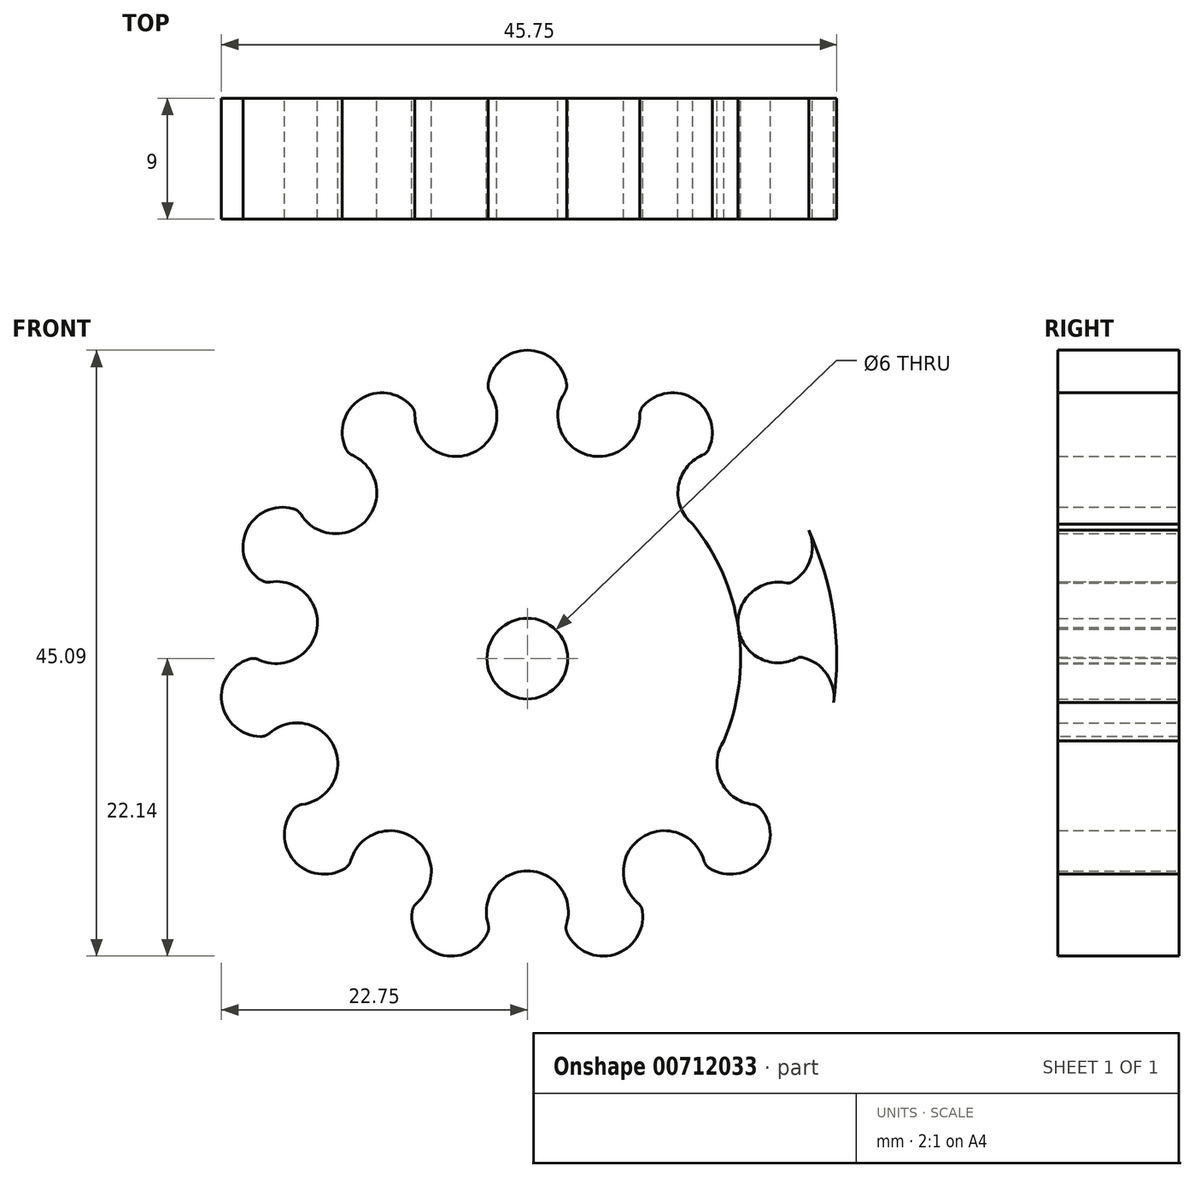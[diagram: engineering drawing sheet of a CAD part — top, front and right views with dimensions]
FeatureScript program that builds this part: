
annotation { "Feature Type Name" : "Feature", "Feature Type Description" : "" }
export const myFeature = defineFeature(function(context is Context, id is Id, definition is map)
    precondition{}
    {
        {
            var Q0;
            Q0=qCreatedBy(makeId("Front.planeOp"),FACE);
            var sketch = newSketch(context, id + "F0", { "sketchPlane" : qUnion([Q0])});
            skCircle(sketch, "E0", {"center": v(0, 0) * mm, "radius": 23 * mm});
            skArc(sketch, "E1", {"start": v(3, 20.2) * mm, "mid": v(0, 23) * mm, "end": v(-3, 20.2) * mm});
            skLineSegment(sketch, "E2", {"start": v(0, 0) * mm, "end": v(0, -23) * mm});
            skLineSegment(sketch, "E3", {"start": v(0, 23) * mm, "end": v(0, 23) * mm});
            skArc(sketch, "E4.1.7", {"start": v(-8.4, 18.61) * mm, "mid": v(-12.43, 19.35) * mm, "end": v(-13.44, 15.37) * mm});
            skArc(sketch, "E4.2.7", {"start": v(-17.13, 11.11) * mm, "mid": v(-20.92, 9.55) * mm, "end": v(-19.62, 5.67) * mm});
            skArc(sketch, "E4.3.7", {"start": v(-20.42, 0.09) * mm, "mid": v(-22.77, -3.27) * mm, "end": v(-19.57, -5.84) * mm});
            skArc(sketch, "E4.4.7", {"start": v(-17.22, -10.96) * mm, "mid": v(-17.38, -15.06) * mm, "end": v(-13.3, -15.49) * mm});
            skArc(sketch, "E4.5.7", {"start": v(-8.56, -18.54) * mm, "mid": v(-6.48, -22.07) * mm, "end": v(-2.82, -20.22) * mm});
            skArc(sketch, "E4.6.7", {"start": v(2.82, -20.22) * mm, "mid": v(6.48, -22.07) * mm, "end": v(8.56, -18.54) * mm});
            skArc(sketch, "E4.7.7", {"start": v(13.3, -15.49) * mm, "mid": v(17.38, -15.06) * mm, "end": v(17.22, -10.96) * mm});
            skCircle(sketch, "E5", {"center": v(0, 0) * mm, "radius": 15.85 * mm});
            skCircle(sketch, "E6", {"center": v(0, 0) * mm, "radius": 3 * mm});
            skArc(sketch, "E7.13.8.0", {"start": v(19.57, -5.84) * mm, "mid": v(22.77, -3.27) * mm, "end": v(20.42, 0.09) * mm});
            skArc(sketch, "E8.13.9.0", {"start": v(19.62, 5.67) * mm, "mid": v(20.92, 9.55) * mm, "end": v(17.13, 11.11) * mm});
            skArc(sketch, "E9.13.10.0", {"start": v(13.44, 15.37) * mm, "mid": v(12.43, 19.35) * mm, "end": v(8.4, 18.61) * mm});
            skArc(sketch, "E10", {"start": v(2.9, 19.87) * mm, "mid": v(4.47, 15.2) * mm, "end": v(8.3, 18.28) * mm});
            skArc(sketch, "E11.1.0", {"start": v(-8.3, 18.28) * mm, "mid": v(-4.47, 15.2) * mm, "end": v(-2.9, 19.87) * mm});
            skArc(sketch, "E11.2.0", {"start": v(-16.87, 10.89) * mm, "mid": v(-11.98, 10.38) * mm, "end": v(-13.18, 15.15) * mm});
            skArc(sketch, "E11.3.0", {"start": v(-20.08, 0.04) * mm, "mid": v(-15.69, 2.26) * mm, "end": v(-19.28, 5.62) * mm});
            skArc(sketch, "E11.4.0", {"start": v(-16.91, -10.82) * mm, "mid": v(-14.42, -6.58) * mm, "end": v(-19.25, -5.7) * mm});
            skArc(sketch, "E11.5.0", {"start": v(-8.38, -18.25) * mm, "mid": v(-8.57, -13.33) * mm, "end": v(-13.12, -15.2) * mm});
            skArc(sketch, "E11.6.0", {"start": v(2.82, -19.88) * mm, "mid": v(0, -15.85) * mm, "end": v(-2.82, -19.88) * mm});
            skArc(sketch, "E11.7.0", {"start": v(13.12, -15.2) * mm, "mid": v(8.57, -13.33) * mm, "end": v(8.38, -18.25) * mm});
            skArc(sketch, "E11.8.0", {"start": v(19.25, -5.7) * mm, "mid": v(14.42, -6.58) * mm, "end": v(16.91, -10.82) * mm});
            skArc(sketch, "E11.9.0", {"start": v(19.28, 5.62) * mm, "mid": v(15.69, 2.26) * mm, "end": v(20.08, 0.04) * mm});
            skArc(sketch, "E11.10.0", {"start": v(13.18, 15.15) * mm, "mid": v(11.98, 10.38) * mm, "end": v(16.87, 10.89) * mm});
            skPoint(sketch, "E12.visualSharp", {"position": v(3, 20) * mm});
            skArc(sketch, "E12.filletArc", {"start": v(2.9, 19.87) * mm, "mid": v(2.97, 20.02) * mm, "end": v(3, 20.2) * mm});
            skPoint(sketch, "E13.visualSharp", {"position": v(-3, 20) * mm});
            skArc(sketch, "E13.filletArc", {"start": v(-3, 20.2) * mm, "mid": v(-2.97, 20.02) * mm, "end": v(-2.9, 19.87) * mm});
            skPoint(sketch, "E14.visualSharp", {"position": v(-8.29, 18.45) * mm});
            skArc(sketch, "E14.filletArc", {"start": v(-8.3, 18.28) * mm, "mid": v(-8.32, 18.45) * mm, "end": v(-8.4, 18.61) * mm});
            skPoint(sketch, "E15.visualSharp", {"position": v(-13.34, 15.2) * mm});
            skArc(sketch, "E15.filletArc", {"start": v(-13.44, 15.37) * mm, "mid": v(-13.33, 15.24) * mm, "end": v(-13.18, 15.15) * mm});
            skPoint(sketch, "E16.visualSharp", {"position": v(-16.95, 11.04) * mm});
            skArc(sketch, "E16.filletArc", {"start": v(-16.87, 10.89) * mm, "mid": v(-16.98, 11.02) * mm, "end": v(-17.13, 11.11) * mm});
            skPoint(sketch, "E17.visualSharp", {"position": v(8.29, 18.45) * mm});
            skArc(sketch, "E17.filletArc", {"start": v(8.4, 18.61) * mm, "mid": v(8.32, 18.45) * mm, "end": v(8.3, 18.28) * mm});
            skPoint(sketch, "E18.visualSharp", {"position": v(13.34, 15.2) * mm});
            skArc(sketch, "E18.filletArc", {"start": v(13.18, 15.15) * mm, "mid": v(13.33, 15.24) * mm, "end": v(13.44, 15.37) * mm});
            skPoint(sketch, "E19.visualSharp", {"position": v(16.95, 11.04) * mm});
            skArc(sketch, "E19.filletArc", {"start": v(17.13, 11.11) * mm, "mid": v(16.98, 11.02) * mm, "end": v(16.87, 10.89) * mm});
            skPoint(sketch, "E20.visualSharp", {"position": v(19.44, 5.58) * mm});
            skArc(sketch, "E20.filletArc", {"start": v(19.28, 5.62) * mm, "mid": v(19.45, 5.61) * mm, "end": v(19.62, 5.67) * mm});
            skPoint(sketch, "E21.visualSharp", {"position": v(20.22, 0.12) * mm});
            skArc(sketch, "E21.filletArc", {"start": v(20.42, 0.09) * mm, "mid": v(20.24, 0.1) * mm, "end": v(20.08, 0.04) * mm});
            skPoint(sketch, "E22.visualSharp", {"position": v(19.37, -5.82) * mm});
            skArc(sketch, "E22.filletArc", {"start": v(19.25, -5.7) * mm, "mid": v(19.4, -5.8) * mm, "end": v(19.57, -5.84) * mm});
            skPoint(sketch, "E23.visualSharp", {"position": v(17.08, -10.83) * mm});
            skArc(sketch, "E23.filletArc", {"start": v(17.22, -10.96) * mm, "mid": v(17.08, -10.87) * mm, "end": v(16.91, -10.82) * mm});
            skPoint(sketch, "E24.visualSharp", {"position": v(13.15, -15.36) * mm});
            skArc(sketch, "E24.filletArc", {"start": v(13.12, -15.2) * mm, "mid": v(13.19, -15.36) * mm, "end": v(13.3, -15.49) * mm});
            skPoint(sketch, "E25.visualSharp", {"position": v(8.51, -18.34) * mm});
            skArc(sketch, "E25.filletArc", {"start": v(8.56, -18.54) * mm, "mid": v(8.5, -18.38) * mm, "end": v(8.38, -18.25) * mm});
            skPoint(sketch, "E26.visualSharp", {"position": v(2.76, -20.04) * mm});
            skArc(sketch, "E26.filletArc", {"start": v(2.82, -19.88) * mm, "mid": v(2.79, -20.05) * mm, "end": v(2.82, -20.22) * mm});
            skPoint(sketch, "E27.visualSharp", {"position": v(-2.76, -20.04) * mm});
            skArc(sketch, "E27.filletArc", {"start": v(-2.82, -20.22) * mm, "mid": v(-2.79, -20.05) * mm, "end": v(-2.82, -19.88) * mm});
            skPoint(sketch, "E28.visualSharp", {"position": v(-8.51, -18.34) * mm});
            skArc(sketch, "E28.filletArc", {"start": v(-8.38, -18.25) * mm, "mid": v(-8.5, -18.38) * mm, "end": v(-8.56, -18.54) * mm});
            skPoint(sketch, "E29.visualSharp", {"position": v(-13.15, -15.36) * mm});
            skArc(sketch, "E29.filletArc", {"start": v(-13.3, -15.49) * mm, "mid": v(-13.19, -15.36) * mm, "end": v(-13.12, -15.2) * mm});
            skPoint(sketch, "E30.visualSharp", {"position": v(-17.08, -10.83) * mm});
            skArc(sketch, "E30.filletArc", {"start": v(-16.91, -10.82) * mm, "mid": v(-17.08, -10.87) * mm, "end": v(-17.22, -10.96) * mm});
            skPoint(sketch, "E31.visualSharp", {"position": v(-19.37, -5.82) * mm});
            skArc(sketch, "E31.filletArc", {"start": v(-19.57, -5.84) * mm, "mid": v(-19.4, -5.8) * mm, "end": v(-19.25, -5.7) * mm});
            skPoint(sketch, "E32.visualSharp", {"position": v(-20.22, 0.12) * mm});
            skArc(sketch, "E32.filletArc", {"start": v(-20.08, 0.04) * mm, "mid": v(-20.24, 0.1) * mm, "end": v(-20.42, 0.09) * mm});
            skPoint(sketch, "E33.visualSharp", {"position": v(-19.44, 5.58) * mm});
            skArc(sketch, "E33.filletArc", {"start": v(-19.62, 5.67) * mm, "mid": v(-19.45, 5.61) * mm, "end": v(-19.28, 5.62) * mm});
            skSolve(sketch);
        }
        {
            var Q0;
            {var subQ1=sQuery(id+"F0.wireOp",EDGE,"E4.1.2");Q0=makeQuery(id+"F0.imprint","IMPRINT",FACE,{"disambiguationData":[TD([[makeQuery(id+"F0.imprint","IMPRINT",EDGE,{"derivedFrom":subQ1}),1.0]])]});}
            var Q1;
            {var subQ1=sQuery(id+"F0.wireOp",EDGE,"E4.2.2");Q1=makeQuery(id+"F0.imprint","IMPRINT",FACE,{"disambiguationData":[TD([[makeQuery(id+"F0.imprint","IMPRINT",EDGE,{"derivedFrom":subQ1}),1.0]])]});}
            var Q2;
            {var subQ1=sQuery(id+"F0.wireOp",EDGE,"E4.3.2");Q2=makeQuery(id+"F0.imprint","IMPRINT",FACE,{"disambiguationData":[TD([[makeQuery(id+"F0.imprint","IMPRINT",EDGE,{"derivedFrom":subQ1}),1.0]])]});}
            var Q3;
            {var subQ1=sQuery(id+"F0.wireOp",EDGE,"E4.4.2");Q3=makeQuery(id+"F0.imprint","IMPRINT",FACE,{"disambiguationData":[TD([[makeQuery(id+"F0.imprint","IMPRINT",EDGE,{"derivedFrom":subQ1}),1.0]])]});}
            var Q4;
            {var subQ1=sQuery(id+"F0.wireOp",EDGE,"E4.5.2");Q4=makeQuery(id+"F0.imprint","IMPRINT",FACE,{"disambiguationData":[TD([[makeQuery(id+"F0.imprint","IMPRINT",EDGE,{"derivedFrom":subQ1}),1.0]])]});}
            var Q5;
            {var subQ1=sQuery(id+"F0.wireOp",EDGE,"E4.6.2");Q5=makeQuery(id+"F0.imprint","IMPRINT",FACE,{"disambiguationData":[TD([[makeQuery(id+"F0.imprint","IMPRINT",EDGE,{"derivedFrom":subQ1}),1.0]])]});}
            var Q6;
            {var subQ1=sQuery(id+"F0.wireOp",EDGE,"E4.7.2");Q6=makeQuery(id+"F0.imprint","IMPRINT",FACE,{"disambiguationData":[TD([[makeQuery(id+"F0.imprint","IMPRINT",EDGE,{"derivedFrom":subQ1}),1.0]])]});}
            var Q7;
            {var subQ1=sQuery(id+"F0.wireOp",EDGE,"E4.8.2");Q7=makeQuery(id+"F0.imprint","IMPRINT",FACE,{"disambiguationData":[TD([[makeQuery(id+"F0.imprint","IMPRINT",EDGE,{"derivedFrom":subQ1}),1.0]])]});}
            var Q8;
            {var subQ1=sQuery(id+"F0.wireOp",EDGE,"064e12d8-6572-4041-806d-f88136f2c4dc");Q8=makeQuery(id+"F0.imprint","IMPRINT",FACE,{"disambiguationData":[TD([[makeQuery(id+"F0.imprint","IMPRINT",EDGE,{"derivedFrom":subQ1}),1.0]])]});}
            var Q9;
            Q9=makeQuery(id+"F0.imprint","IMPRINT",FACE,{"disambiguationData":[TD([[makeQuery(id+"F0.imprint","IMPRINT",EDGE,{"derivedFrom":sQuery(id+"F0.wireOp",EDGE,"E6")}),-1.0]])]});
            var Q10;
            {var subQ0=sQuery(id+"F0.wireOp",EDGE,"E4.4.3");Q10=makeQuery(id+"F0.imprint","IMPRINT",FACE,{"disambiguationData":[TD([[makeQuery(id+"F0.imprint","IMPRINT",EDGE,{"derivedFrom":subQ0}),-1.0]])]});}
            var Q11;
            {var subQ5=sQuery(id+"F0.wireOp",EDGE,"E7.2.8.0");Q11=makeQuery(id+"F0.imprint","IMPRINT",FACE,{"disambiguationData":[TD([[makeQuery(id+"F0.imprint","IMPRINT",EDGE,{"derivedFrom":subQ5}),1.0]])]});}
            var Q12;
            {var subQ0=sQuery(id+"F0.wireOp",EDGE,"E4.5.3");Q12=makeQuery(id+"F0.imprint","IMPRINT",FACE,{"disambiguationData":[TD([[makeQuery(id+"F0.imprint","IMPRINT",EDGE,{"derivedFrom":subQ0}),-1.0]])]});}
            var Q13;
            {var subQ1=sQuery(id+"F0.wireOp",EDGE,"E8.2.9.0");Q13=makeQuery(id+"F0.imprint","IMPRINT",FACE,{"disambiguationData":[TD([[makeQuery(id+"F0.imprint","IMPRINT",EDGE,{"derivedFrom":subQ1}),1.0]])]});}
            var Q14;
            {var subQ2=sQuery(id+"F0.wireOp",EDGE,"E9.2.10.0");Q14=makeQuery(id+"F0.imprint","IMPRINT",FACE,{"disambiguationData":[TD([[makeQuery(id+"F0.imprint","IMPRINT",EDGE,{"derivedFrom":subQ2}),1.0]])]});}
            var Q15;
            {var subQ0=sQuery(id+"F0.wireOp",EDGE,"E11.9.0");var subQ3=sQuery(id+"F0.wireOp",EDGE,"E5");var subQ4=makeQuery(id+"F0.imprint","INTERSECT",VERTEX,{"disambiguationData":[OD(0.0)],"derivedFrom":[subQ3,subQ0]});Q15=makeQuery(id+"F0.imprint","IMPRINT",FACE,{"disambiguationData":[TD([[makeQuery(id+"F0.imprint","IMPRINT",EDGE,{"disambiguationData":[TD([[subQ4,-1.0]])],"derivedFrom":subQ3}),-1.0]])]});}
            var Q16;
            {var subQ3=sQuery(id+"F0.wireOp",EDGE,"E5");var subQ6=sQuery(id+"F0.wireOp",EDGE,"E11.10.0");var subQ8=makeQuery(id+"F0.imprint","INTERSECT",VERTEX,{"disambiguationData":[OD(1.0)],"derivedFrom":[subQ3,subQ6]});Q16=makeQuery(id+"F0.imprint","IMPRINT",FACE,{"disambiguationData":[TD([[makeQuery(id+"F0.imprint","IMPRINT",EDGE,{"disambiguationData":[TD([[subQ8,-1.0]])],"derivedFrom":subQ3}),-1.0]])]});}
            var Q17;
            {var subQ0=sQuery(id+"F0.wireOp",EDGE,"E10");var subQ1=sQuery(id+"F0.wireOp",EDGE,"E1");var subQ2=makeQuery(id+"F0.imprint","INTERSECT",VERTEX,{"derivedFrom":[subQ1,subQ0]});Q17=makeQuery(id+"F0.imprint","IMPRINT",FACE,{"disambiguationData":[TD([[makeQuery(id+"F0.imprint","IMPRINT",EDGE,{"disambiguationData":[TD([[subQ2,-1.0]])],"derivedFrom":subQ1}),1.0]])]});}
            var Q18;
            {var subQ0=sQuery(id+"F0.wireOp",EDGE,"E11.1.0");var subQ1=sQuery(id+"F0.wireOp",EDGE,"E4.1.7");var subQ2=makeQuery(id+"F0.imprint","INTERSECT",VERTEX,{"derivedFrom":[subQ1,subQ0]});Q18=makeQuery(id+"F0.imprint","IMPRINT",FACE,{"disambiguationData":[TD([[makeQuery(id+"F0.imprint","IMPRINT",EDGE,{"disambiguationData":[TD([[subQ2,-1.0]])],"derivedFrom":subQ1}),1.0]])]});}
            var Q19;
            {var subQ0=sQuery(id+"F0.wireOp",EDGE,"E11.2.0");var subQ1=sQuery(id+"F0.wireOp",EDGE,"E4.2.7");var subQ2=makeQuery(id+"F0.imprint","INTERSECT",VERTEX,{"derivedFrom":[subQ1,subQ0]});Q19=makeQuery(id+"F0.imprint","IMPRINT",FACE,{"disambiguationData":[TD([[makeQuery(id+"F0.imprint","IMPRINT",EDGE,{"disambiguationData":[TD([[subQ2,-1.0]])],"derivedFrom":subQ1}),1.0]])]});}
            var Q20;
            {var subQ0=sQuery(id+"F0.wireOp",EDGE,"E11.3.0");var subQ1=sQuery(id+"F0.wireOp",EDGE,"E4.3.7");var subQ2=makeQuery(id+"F0.imprint","INTERSECT",VERTEX,{"derivedFrom":[subQ1,subQ0]});Q20=makeQuery(id+"F0.imprint","IMPRINT",FACE,{"disambiguationData":[TD([[makeQuery(id+"F0.imprint","IMPRINT",EDGE,{"disambiguationData":[TD([[subQ2,-1.0]])],"derivedFrom":subQ1}),1.0]])]});}
            var Q21;
            {var subQ0=sQuery(id+"F0.wireOp",EDGE,"E11.4.0");var subQ5=sQuery(id+"F0.wireOp",EDGE,"E4.4.7");var subQ8=makeQuery(id+"F0.imprint","INTERSECT",VERTEX,{"derivedFrom":[subQ5,subQ0]});Q21=makeQuery(id+"F0.imprint","IMPRINT",FACE,{"disambiguationData":[TD([[makeQuery(id+"F0.imprint","IMPRINT",EDGE,{"disambiguationData":[TD([[subQ8,-1.0]])],"derivedFrom":subQ5}),1.0]])]});}
            var Q22;
            {var subQ0=sQuery(id+"F0.wireOp",EDGE,"E11.5.0");var subQ1=sQuery(id+"F0.wireOp",EDGE,"E4.5.7");var subQ2=makeQuery(id+"F0.imprint","INTERSECT",VERTEX,{"derivedFrom":[subQ1,subQ0]});Q22=makeQuery(id+"F0.imprint","IMPRINT",FACE,{"disambiguationData":[TD([[makeQuery(id+"F0.imprint","IMPRINT",EDGE,{"disambiguationData":[TD([[subQ2,-1.0]])],"derivedFrom":subQ1}),1.0]])]});}
            var Q23;
            {var subQ0=sQuery(id+"F0.wireOp",EDGE,"E11.6.0");var subQ1=sQuery(id+"F0.wireOp",EDGE,"E4.6.7");var subQ2=makeQuery(id+"F0.imprint","INTERSECT",VERTEX,{"derivedFrom":[subQ1,subQ0]});Q23=makeQuery(id+"F0.imprint","IMPRINT",FACE,{"disambiguationData":[TD([[makeQuery(id+"F0.imprint","IMPRINT",EDGE,{"disambiguationData":[TD([[subQ2,-1.0]])],"derivedFrom":subQ1}),1.0]])]});}
            var Q24;
            {var subQ0=sQuery(id+"F0.wireOp",EDGE,"E11.7.0");var subQ1=sQuery(id+"F0.wireOp",EDGE,"E4.7.7");var subQ2=makeQuery(id+"F0.imprint","INTERSECT",VERTEX,{"derivedFrom":[subQ1,subQ0]});Q24=makeQuery(id+"F0.imprint","IMPRINT",FACE,{"disambiguationData":[TD([[makeQuery(id+"F0.imprint","IMPRINT",EDGE,{"disambiguationData":[TD([[subQ2,-1.0]])],"derivedFrom":subQ1}),1.0]])]});}
            var Q25;
            {var subQ3=sQuery(id+"F0.wireOp",EDGE,"E5");var subQ5=sQuery(id+"F0.wireOp",EDGE,"E11.9.0");var subQ6=makeQuery(id+"F0.imprint","INTERSECT",VERTEX,{"disambiguationData":[OD(1.0)],"derivedFrom":[subQ3,subQ5]});Q25=makeQuery(id+"F0.imprint","IMPRINT",FACE,{"disambiguationData":[TD([[makeQuery(id+"F0.imprint","IMPRINT",EDGE,{"disambiguationData":[TD([[subQ6,1.0]])],"derivedFrom":subQ3}),-1.0]])]});}
            extrude(context, id + "F1", {"entities" : qUnion([Q0, Q1, Q2, Q3, Q4, Q5, Q6, Q7, Q8, Q9, Q10, Q11, Q12, Q13, Q14, Q15, Q16, Q17, Q18, Q19, Q20, Q21, Q22, Q23, Q24, Q25]), "depth" : 9 * mm, "offsetDistance" : 25 * mm});
        }
        {
            var Q0;
            Q0=makeQuery(id+"F1.opExtrude","CAP_FACE",FACE,{"disambiguationData":[OSD([sQuery(id+"F0.wireOp",EDGE,"E1"),sQuery(id+"F0.wireOp",EDGE,"E4.1.7"),sQuery(id+"F0.wireOp",EDGE,"E4.2.7"),sQuery(id+"F0.wireOp",EDGE,"E4.3.7"),sQuery(id+"F0.wireOp",EDGE,"E4.4.7"),sQuery(id+"F0.wireOp",EDGE,"E4.5.7"),sQuery(id+"F0.wireOp",EDGE,"E4.6.7"),sQuery(id+"F0.wireOp",EDGE,"E4.7.7"),sQuery(id+"F0.wireOp",EDGE,"E6"),sQuery(id+"F0.wireOp",EDGE,"E7.13.8.0"),sQuery(id+"F0.wireOp",EDGE,"E8.13.9.0"),sQuery(id+"F0.wireOp",EDGE,"E9.13.10.0"),sQuery(id+"F0.wireOp",EDGE,"E10"),sQuery(id+"F0.wireOp",EDGE,"E11.1.0"),sQuery(id+"F0.wireOp",EDGE,"E11.2.0"),sQuery(id+"F0.wireOp",EDGE,"E11.3.0"),sQuery(id+"F0.wireOp",EDGE,"E11.4.0"),sQuery(id+"F0.wireOp",EDGE,"E11.5.0"),sQuery(id+"F0.wireOp",EDGE,"E11.6.0"),sQuery(id+"F0.wireOp",EDGE,"E11.7.0"),sQuery(id+"F0.wireOp",EDGE,"E11.8.0"),sQuery(id+"F0.wireOp",EDGE,"E11.9.0"),sQuery(id+"F0.wireOp",EDGE,"E11.10.0"),sQuery(id+"F0.wireOp",EDGE,"E12.filletArc"),sQuery(id+"F0.wireOp",EDGE,"E13.filletArc"),sQuery(id+"F0.wireOp",EDGE,"E14.filletArc"),sQuery(id+"F0.wireOp",EDGE,"E15.filletArc"),sQuery(id+"F0.wireOp",EDGE,"E16.filletArc"),sQuery(id+"F0.wireOp",EDGE,"E17.filletArc"),sQuery(id+"F0.wireOp",EDGE,"E18.filletArc"),sQuery(id+"F0.wireOp",EDGE,"E19.filletArc"),sQuery(id+"F0.wireOp",EDGE,"E20.filletArc"),sQuery(id+"F0.wireOp",EDGE,"E21.filletArc"),sQuery(id+"F0.wireOp",EDGE,"E22.filletArc"),sQuery(id+"F0.wireOp",EDGE,"E23.filletArc"),sQuery(id+"F0.wireOp",EDGE,"E24.filletArc"),sQuery(id+"F0.wireOp",EDGE,"E25.filletArc"),sQuery(id+"F0.wireOp",EDGE,"E26.filletArc"),sQuery(id+"F0.wireOp",EDGE,"E27.filletArc"),sQuery(id+"F0.wireOp",EDGE,"E28.filletArc"),sQuery(id+"F0.wireOp",EDGE,"E29.filletArc"),sQuery(id+"F0.wireOp",EDGE,"E30.filletArc"),sQuery(id+"F0.wireOp",EDGE,"E31.filletArc"),sQuery(id+"F0.wireOp",EDGE,"E32.filletArc"),sQuery(id+"F0.wireOp",EDGE,"E33.filletArc")])],"isStart":true});
            var sketch = newSketch(context, id + "F2", { "sketchPlane" : qUnion([Q0])});
            skArc(sketch, "E34.0", {"start": v(-2.9, 19.87) * mm, "mid": v(-4.47, 15.2) * mm, "end": v(-8.3, 18.28) * mm});
            skArc(sketch, "E35.0", {"start": v(-3, 20.2) * mm, "mid": v(0, 23) * mm, "end": v(3, 20.2) * mm});
            skArc(sketch, "E36.0", {"start": v(8.3, 18.28) * mm, "mid": v(4.47, 15.2) * mm, "end": v(2.9, 19.87) * mm});
            skArc(sketch, "E37.0", {"start": v(8.4, 18.61) * mm, "mid": v(12.43, 19.35) * mm, "end": v(13.44, 15.37) * mm});
            skArc(sketch, "E38.0", {"start": v(16.87, 10.89) * mm, "mid": v(11.98, 10.38) * mm, "end": v(13.18, 15.15) * mm});
            skArc(sketch, "E39.0", {"start": v(17.13, 11.11) * mm, "mid": v(20.92, 9.55) * mm, "end": v(19.62, 5.67) * mm});
            skArc(sketch, "E40.0", {"start": v(20.08, 0.04) * mm, "mid": v(15.69, 2.26) * mm, "end": v(19.28, 5.62) * mm});
            skArc(sketch, "E41.0", {"start": v(20.42, 0.09) * mm, "mid": v(22.77, -3.27) * mm, "end": v(19.57, -5.84) * mm});
            skArc(sketch, "E42.0", {"start": v(16.91, -10.82) * mm, "mid": v(14.42, -6.58) * mm, "end": v(19.25, -5.7) * mm});
            skArc(sketch, "E43.0", {"start": v(17.22, -10.96) * mm, "mid": v(17.38, -15.06) * mm, "end": v(13.3, -15.49) * mm});
            skArc(sketch, "E44.0", {"start": v(8.38, -18.25) * mm, "mid": v(8.57, -13.33) * mm, "end": v(13.12, -15.2) * mm});
            skArc(sketch, "E45.0", {"start": v(8.56, -18.54) * mm, "mid": v(6.48, -22.07) * mm, "end": v(2.82, -20.22) * mm});
            skArc(sketch, "E46.0", {"start": v(-2.82, -19.88) * mm, "mid": v(0, -15.85) * mm, "end": v(2.82, -19.88) * mm});
            skArc(sketch, "E47.0", {"start": v(-2.82, -20.22) * mm, "mid": v(-6.48, -22.07) * mm, "end": v(-8.56, -18.54) * mm});
            skArc(sketch, "E48.0", {"start": v(-13.12, -15.2) * mm, "mid": v(-8.57, -13.33) * mm, "end": v(-8.38, -18.25) * mm});
            skArc(sketch, "E49.0", {"start": v(-13.3, -15.49) * mm, "mid": v(-17.38, -15.06) * mm, "end": v(-17.22, -10.96) * mm});
            skArc(sketch, "E50.0", {"start": v(-19.25, -5.7) * mm, "mid": v(-14.42, -6.58) * mm, "end": v(-16.91, -10.82) * mm});
            skArc(sketch, "E51.0", {"start": v(-19.57, -5.84) * mm, "mid": v(-22.77, -3.27) * mm, "end": v(-20.42, 0.09) * mm});
            skArc(sketch, "E52.0", {"start": v(-19.28, 5.62) * mm, "mid": v(-15.69, 2.26) * mm, "end": v(-20.08, 0.04) * mm});
            skArc(sketch, "E53.0", {"start": v(-13.18, 15.15) * mm, "mid": v(-11.98, 10.38) * mm, "end": v(-16.87, 10.89) * mm});
            skArc(sketch, "E54.0", {"start": v(-13.44, 15.37) * mm, "mid": v(-12.43, 19.35) * mm, "end": v(-8.4, 18.61) * mm});
            skArc(sketch, "E55.0", {"start": v(-19.62, 5.67) * mm, "mid": v(-20.92, 9.55) * mm, "end": v(-17.13, 11.11) * mm});
            skArc(sketch, "E56.0", {"start": v(-13.18, 15.15) * mm, "mid": v(-13.33, 15.24) * mm, "end": v(-13.44, 15.37) * mm});
            skArc(sketch, "E57.0", {"start": v(-8.4, 18.61) * mm, "mid": v(-8.32, 18.45) * mm, "end": v(-8.3, 18.28) * mm});
            skPoint(sketch, "E58.0", {"position": v(-2.97, 20.02) * mm});
            skArc(sketch, "E59.0", {"start": v(3, 20.2) * mm, "mid": v(2.97, 20.02) * mm, "end": v(2.9, 19.87) * mm});
            skArc(sketch, "E60.0", {"start": v(13.44, 15.37) * mm, "mid": v(13.33, 15.24) * mm, "end": v(13.18, 15.15) * mm});
            skArc(sketch, "E61.0", {"start": v(8.3, 18.28) * mm, "mid": v(8.32, 18.45) * mm, "end": v(8.4, 18.61) * mm});
            skPoint(sketch, "E62.0", {"position": v(16.98, 11.02) * mm});
            skArc(sketch, "E63.0", {"start": v(19.62, 5.67) * mm, "mid": v(19.45, 5.61) * mm, "end": v(19.28, 5.62) * mm});
            skArc(sketch, "E64.0", {"start": v(16.87, 10.89) * mm, "mid": v(16.98, 11.02) * mm, "end": v(17.13, 11.11) * mm});
            skArc(sketch, "E65.0", {"start": v(-2.9, 19.87) * mm, "mid": v(-2.97, 20.02) * mm, "end": v(-3, 20.2) * mm});
            skArc(sketch, "E66.0", {"start": v(-19.28, 5.62) * mm, "mid": v(-19.45, 5.61) * mm, "end": v(-19.62, 5.67) * mm});
            skArc(sketch, "E67.0", {"start": v(-17.13, 11.11) * mm, "mid": v(-16.98, 11.02) * mm, "end": v(-16.87, 10.89) * mm});
            skArc(sketch, "E68.0", {"start": v(-19.25, -5.7) * mm, "mid": v(-19.4, -5.8) * mm, "end": v(-19.57, -5.84) * mm});
            skArc(sketch, "E69.0", {"start": v(-20.42, 0.09) * mm, "mid": v(-20.24, 0.1) * mm, "end": v(-20.08, 0.04) * mm});
            skArc(sketch, "E70.0", {"start": v(-17.22, -10.96) * mm, "mid": v(-17.08, -10.87) * mm, "end": v(-16.91, -10.82) * mm});
            skArc(sketch, "E71.0", {"start": v(-13.12, -15.2) * mm, "mid": v(-13.19, -15.36) * mm, "end": v(-13.3, -15.49) * mm});
            skArc(sketch, "E72.0", {"start": v(-8.56, -18.54) * mm, "mid": v(-8.5, -18.38) * mm, "end": v(-8.38, -18.25) * mm});
            skArc(sketch, "E73.0", {"start": v(-2.82, -19.88) * mm, "mid": v(-2.79, -20.05) * mm, "end": v(-2.82, -20.22) * mm});
            skArc(sketch, "E74.0", {"start": v(2.82, -20.22) * mm, "mid": v(2.79, -20.05) * mm, "end": v(2.82, -19.88) * mm});
            skArc(sketch, "E75.0", {"start": v(8.38, -18.25) * mm, "mid": v(8.5, -18.38) * mm, "end": v(8.56, -18.54) * mm});
            skArc(sketch, "E76.0", {"start": v(13.3, -15.49) * mm, "mid": v(13.19, -15.36) * mm, "end": v(13.12, -15.2) * mm});
            skArc(sketch, "E77.0", {"start": v(16.91, -10.82) * mm, "mid": v(17.08, -10.87) * mm, "end": v(17.22, -10.96) * mm});
            skArc(sketch, "E78.0", {"start": v(19.57, -5.84) * mm, "mid": v(19.4, -5.8) * mm, "end": v(19.25, -5.7) * mm});
            skArc(sketch, "E79.0", {"start": v(20.08, 0.04) * mm, "mid": v(20.24, 0.1) * mm, "end": v(20.42, 0.09) * mm});
            skArc(sketch, "E80.0", {"start": v(-2.95, 20.02) * mm, "mid": v(0, 22.95) * mm, "end": v(2.95, 20.02) * mm});
            skArc(sketch, "E80.1", {"start": v(8.34, 18.43) * mm, "mid": v(4.45, 15.16) * mm, "end": v(2.95, 20.02) * mm});
            skArc(sketch, "E80.2", {"start": v(8.34, 18.43) * mm, "mid": v(12.4, 19.3) * mm, "end": v(13.3, 15.25) * mm});
            skArc(sketch, "E80.3", {"start": v(16.98, 11) * mm, "mid": v(11.94, 10.35) * mm, "end": v(13.3, 15.25) * mm});
            skArc(sketch, "E80.4", {"start": v(16.98, 11) * mm, "mid": v(20.88, 9.53) * mm, "end": v(19.43, 5.63) * mm});
            skArc(sketch, "E80.5", {"start": v(-2.95, 20.02) * mm, "mid": v(-4.45, 15.16) * mm, "end": v(-8.34, 18.43) * mm});
            skArc(sketch, "E80.6", {"start": v(20.23, 0.07) * mm, "mid": v(15.64, 2.25) * mm, "end": v(19.43, 5.63) * mm});
            skArc(sketch, "E80.7", {"start": v(20.23, 0.07) * mm, "mid": v(22.72, -3.27) * mm, "end": v(19.4, -5.77) * mm});
            skArc(sketch, "E80.8", {"start": v(17.06, -10.88) * mm, "mid": v(14.37, -6.56) * mm, "end": v(19.4, -5.77) * mm});
            skArc(sketch, "E80.9", {"start": v(17.06, -10.88) * mm, "mid": v(17.34, -15.03) * mm, "end": v(13.2, -15.34) * mm});
            skArc(sketch, "E80.10", {"start": v(8.47, -18.38) * mm, "mid": v(8.54, -13.3) * mm, "end": v(13.2, -15.34) * mm});
            skArc(sketch, "E80.11", {"start": v(8.47, -18.38) * mm, "mid": v(6.47, -22.02) * mm, "end": v(2.8, -20.04) * mm});
            skArc(sketch, "E80.12", {"start": v(-19.43, 5.63) * mm, "mid": v(-15.64, 2.25) * mm, "end": v(-20.23, 0.07) * mm});
            skArc(sketch, "E80.13", {"start": v(-19.43, 5.63) * mm, "mid": v(-20.88, 9.53) * mm, "end": v(-16.98, 11) * mm});
            skArc(sketch, "E80.14", {"start": v(-13.3, 15.25) * mm, "mid": v(-11.94, 10.35) * mm, "end": v(-16.98, 11) * mm});
            skArc(sketch, "E80.15", {"start": v(-13.3, 15.25) * mm, "mid": v(-12.4, 19.3) * mm, "end": v(-8.34, 18.43) * mm});
            skArc(sketch, "E80.16", {"start": v(-19.4, -5.77) * mm, "mid": v(-22.72, -3.27) * mm, "end": v(-20.23, 0.07) * mm});
            skArc(sketch, "E80.17", {"start": v(-19.4, -5.77) * mm, "mid": v(-14.37, -6.56) * mm, "end": v(-17.06, -10.88) * mm});
            skArc(sketch, "E80.18", {"start": v(-13.2, -15.34) * mm, "mid": v(-17.34, -15.03) * mm, "end": v(-17.06, -10.88) * mm});
            skArc(sketch, "E80.19", {"start": v(-13.2, -15.34) * mm, "mid": v(-8.54, -13.3) * mm, "end": v(-8.47, -18.38) * mm});
            skArc(sketch, "E80.20", {"start": v(-2.8, -20.04) * mm, "mid": v(-6.47, -22.02) * mm, "end": v(-8.47, -18.38) * mm});
            skArc(sketch, "E80.21", {"start": v(-2.8, -20.04) * mm, "mid": v(0, -15.8) * mm, "end": v(2.8, -20.04) * mm});
            skSolve(sketch);
        }
        {
            var Q0;
            Q0=makeQuery(id+"F2.imprint","IMPRINT",FACE,{"disambiguationData":[TD([[makeQuery(id+"F2.imprint","IMPRINT",EDGE,{"derivedFrom":sQuery(id+"F2.wireOp",EDGE,"E34.0")}),1.0]])]});
            extrude(context, id + "F3", {"entities" : qUnion([Q0]), "operationType" : NewBodyOperationType.REMOVE, "oppositeDirection" : true, "depth" : 25 * mm, "offsetDistance" : 25 * mm});
        }
        {
            var Q0;
            Q0=makeQuery(id+"F3.boolean.opBoolean","COPY",EDGE,{"derivedFrom":makeQuery(id+"F3.opExtrude","SWEPT_EDGE",EDGE,{"disambiguationData":[OSD([sQuery(id+"F2.wireOp",EDGE,"E80.12"),sQuery(id+"F2.wireOp",EDGE,"E80.13")])]})});
            var Q1;
            Q1=makeQuery(id+"F3.boolean.opBoolean","COPY",EDGE,{"derivedFrom":makeQuery(id+"F3.opExtrude","SWEPT_EDGE",EDGE,{"disambiguationData":[OSD([sQuery(id+"F2.wireOp",EDGE,"E80.16"),sQuery(id+"F2.wireOp",EDGE,"E80.17")])]})});
            var Q2;
            Q2=makeQuery(id+"F3.boolean.opBoolean","COPY",EDGE,{"derivedFrom":makeQuery(id+"F3.opExtrude","SWEPT_EDGE",EDGE,{"disambiguationData":[OSD([sQuery(id+"F2.wireOp",EDGE,"E80.14"),sQuery(id+"F2.wireOp",EDGE,"E80.15")])]})});
            var Q3;
            Q3=makeQuery(id+"F3.boolean.opBoolean","COPY",EDGE,{"derivedFrom":makeQuery(id+"F3.opExtrude","SWEPT_EDGE",EDGE,{"disambiguationData":[OSD([sQuery(id+"F2.wireOp",EDGE,"E80.18"),sQuery(id+"F2.wireOp",EDGE,"E80.19")])]})});
            var Q4;
            Q4=makeQuery(id+"F3.boolean.opBoolean","COPY",EDGE,{"derivedFrom":makeQuery(id+"F3.opExtrude","SWEPT_EDGE",EDGE,{"disambiguationData":[OSD([sQuery(id+"F2.wireOp",EDGE,"E80.9"),sQuery(id+"F2.wireOp",EDGE,"E80.10")])]})});
            var Q5;
            Q5=makeQuery(id+"F3.boolean.opBoolean","COPY",EDGE,{"derivedFrom":makeQuery(id+"F3.opExtrude","SWEPT_EDGE",EDGE,{"disambiguationData":[OSD([sQuery(id+"F2.wireOp",EDGE,"E80.7"),sQuery(id+"F2.wireOp",EDGE,"E80.8")])]})});
            var Q6;
            Q6=makeQuery(id+"F3.boolean.opBoolean","COPY",EDGE,{"derivedFrom":makeQuery(id+"F3.opExtrude","SWEPT_EDGE",EDGE,{"disambiguationData":[OSD([sQuery(id+"F2.wireOp",EDGE,"E80.4"),sQuery(id+"F2.wireOp",EDGE,"E80.6")])]})});
            var Q7;
            Q7=makeQuery(id+"F3.boolean.opBoolean","COPY",EDGE,{"derivedFrom":makeQuery(id+"F3.opExtrude","SWEPT_EDGE",EDGE,{"disambiguationData":[OSD([sQuery(id+"F2.wireOp",EDGE,"E80.2"),sQuery(id+"F2.wireOp",EDGE,"E80.3")])]})});
            var Q8;
            Q8=makeQuery(id+"F3.boolean.opBoolean","COPY",EDGE,{"derivedFrom":makeQuery(id+"F3.opExtrude","SWEPT_EDGE",EDGE,{"disambiguationData":[OSD([sQuery(id+"F2.wireOp",EDGE,"E80.0"),sQuery(id+"F2.wireOp",EDGE,"E80.5")])]})});
            var Q9;
            Q9=makeQuery(id+"F3.boolean.opBoolean","COPY",EDGE,{"derivedFrom":makeQuery(id+"F3.opExtrude","SWEPT_EDGE",EDGE,{"disambiguationData":[OSD([sQuery(id+"F2.wireOp",EDGE,"E80.1"),sQuery(id+"F2.wireOp",EDGE,"E80.2")])]})});
            var Q10;
            Q10=makeQuery(id+"F3.boolean.opBoolean","COPY",EDGE,{"derivedFrom":makeQuery(id+"F3.opExtrude","SWEPT_EDGE",EDGE,{"disambiguationData":[OSD([sQuery(id+"F2.wireOp",EDGE,"E80.19"),sQuery(id+"F2.wireOp",EDGE,"E80.20")])]})});
            var Q11;
            Q11=makeQuery(id+"F3.boolean.opBoolean","COPY",EDGE,{"derivedFrom":makeQuery(id+"F3.opExtrude","SWEPT_EDGE",EDGE,{"disambiguationData":[OSD([sQuery(id+"F2.wireOp",EDGE,"E80.11"),sQuery(id+"F2.wireOp",EDGE,"E80.21")])]})});
            var Q12;
            Q12=makeQuery(id+"F3.boolean.opBoolean","COPY",EDGE,{"derivedFrom":makeQuery(id+"F3.opExtrude","SWEPT_EDGE",EDGE,{"disambiguationData":[OSD([sQuery(id+"F2.wireOp",EDGE,"E80.6"),sQuery(id+"F2.wireOp",EDGE,"E80.7")])]})});
            var Q13;
            Q13=makeQuery(id+"F3.boolean.opBoolean","COPY",EDGE,{"derivedFrom":makeQuery(id+"F3.opExtrude","SWEPT_EDGE",EDGE,{"disambiguationData":[OSD([sQuery(id+"F2.wireOp",EDGE,"E80.3"),sQuery(id+"F2.wireOp",EDGE,"E80.4")])]})});
            var Q14;
            Q14=makeQuery(id+"F3.boolean.opBoolean","COPY",EDGE,{"derivedFrom":makeQuery(id+"F3.opExtrude","SWEPT_EDGE",EDGE,{"disambiguationData":[OSD([sQuery(id+"F2.wireOp",EDGE,"E80.17"),sQuery(id+"F2.wireOp",EDGE,"E80.18")])]})});
            var Q15;
            Q15=makeQuery(id+"F3.boolean.opBoolean","COPY",EDGE,{"derivedFrom":makeQuery(id+"F3.opExtrude","SWEPT_EDGE",EDGE,{"disambiguationData":[OSD([sQuery(id+"F2.wireOp",EDGE,"E80.12"),sQuery(id+"F2.wireOp",EDGE,"E80.16")])]})});
            var Q16;
            Q16=makeQuery(id+"F3.boolean.opBoolean","COPY",EDGE,{"derivedFrom":makeQuery(id+"F3.opExtrude","SWEPT_EDGE",EDGE,{"disambiguationData":[OSD([sQuery(id+"F2.wireOp",EDGE,"E80.13"),sQuery(id+"F2.wireOp",EDGE,"E80.14")])]})});
            var Q17;
            Q17=makeQuery(id+"F3.boolean.opBoolean","COPY",EDGE,{"derivedFrom":makeQuery(id+"F3.opExtrude","SWEPT_EDGE",EDGE,{"disambiguationData":[OSD([sQuery(id+"F2.wireOp",EDGE,"E80.5"),sQuery(id+"F2.wireOp",EDGE,"E80.15")])]})});
            var Q18;
            Q18=makeQuery(id+"F3.boolean.opBoolean","COPY",EDGE,{"derivedFrom":makeQuery(id+"F3.opExtrude","SWEPT_EDGE",EDGE,{"disambiguationData":[OSD([sQuery(id+"F2.wireOp",EDGE,"E80.0"),sQuery(id+"F2.wireOp",EDGE,"E80.1")])]})});
            var Q19;
            Q19=makeQuery(id+"F3.boolean.opBoolean","COPY",EDGE,{"derivedFrom":makeQuery(id+"F3.opExtrude","SWEPT_EDGE",EDGE,{"disambiguationData":[OSD([sQuery(id+"F2.wireOp",EDGE,"E80.20"),sQuery(id+"F2.wireOp",EDGE,"E80.21")])]})});
            var Q20;
            Q20=makeQuery(id+"F3.boolean.opBoolean","COPY",EDGE,{"derivedFrom":makeQuery(id+"F3.opExtrude","SWEPT_EDGE",EDGE,{"disambiguationData":[OSD([sQuery(id+"F2.wireOp",EDGE,"E80.10"),sQuery(id+"F2.wireOp",EDGE,"E80.11")])]})});
            var Q21;
            Q21=makeQuery(id+"F3.boolean.opBoolean","COPY",EDGE,{"derivedFrom":makeQuery(id+"F3.opExtrude","SWEPT_EDGE",EDGE,{"disambiguationData":[OSD([sQuery(id+"F2.wireOp",EDGE,"E80.8"),sQuery(id+"F2.wireOp",EDGE,"E80.9")])]})});
            fillet(context, id + "F4", {"entities" : qUnion([Q0, Q1, Q2, Q3, Q4, Q5, Q6, Q7, Q8, Q9, Q10, Q11, Q12, Q13, Q14, Q15, Q16, Q17, Q18, Q19, Q20, Q21]), "radius" : 1 * mm, "tangentPropagation" : true, "allowEdgeOverflow" : false});
        }
    });
